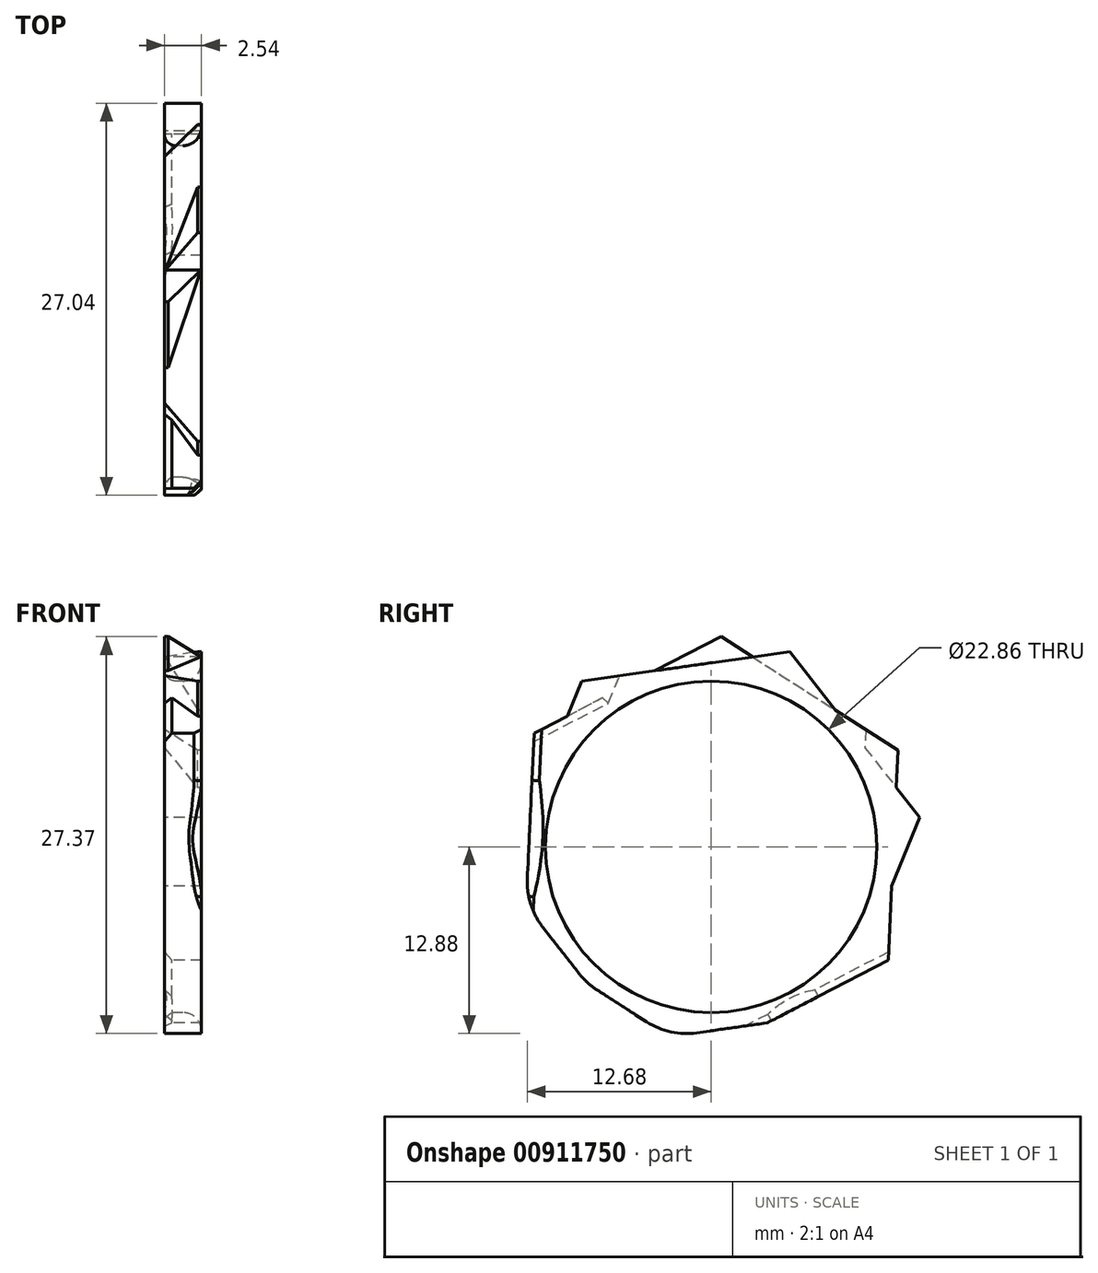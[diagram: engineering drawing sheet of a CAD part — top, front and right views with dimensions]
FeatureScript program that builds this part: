
annotation { "Feature Type Name" : "Feature", "Feature Type Description" : "" }
export const myFeature = defineFeature(function(context is Context, id is Id, definition is map)
    precondition{}
    {
        {
            var Q0;
            Q0=qCreatedBy(makeId("Right.planeOp"),FACE);
            var sketch = newSketch(context, id + "F0", { "sketchPlane" : qUnion([Q0])});
            skCircle(sketch, "E0", {"center": v(0, 0) * mm, "radius": 11.43 * mm});
            skCircle(sketch, "E1.cCircle", {"center": v(0, 0) * mm, "radius": 12.56 * mm, "construction": true});
            skLineSegment(sketch, "E1.0", {"start": v(0.68, 14.49) * mm, "end": v(12.89, 6.66) * mm});
            skLineSegment(sketch, "E1.1", {"start": v(12.89, 6.66) * mm, "end": v(12.2, -7.83) * mm});
            skLineSegment(sketch, "E1.2", {"start": v(12.2, -7.83) * mm, "end": v(-0.68, -14.49) * mm});
            skLineSegment(sketch, "E1.3", {"start": v(-0.68, -14.49) * mm, "end": v(-12.89, -6.66) * mm});
            skLineSegment(sketch, "E1.4", {"start": v(-12.89, -6.66) * mm, "end": v(-12.2, 7.83) * mm});
            skLineSegment(sketch, "E1.5", {"start": v(-12.2, 7.83) * mm, "end": v(0.68, 14.49) * mm});
            skPoint(sketch, "E1.0.midPoint", {"position": v(6.78, 10.57) * mm});
            skLineSegment(sketch, "E2.0", {"start": v(-8.94, 11.42) * mm, "end": v(5.42, 13.45) * mm});
            skLineSegment(sketch, "E2.1", {"start": v(5.42, 13.45) * mm, "end": v(14.36, 2.04) * mm});
            skLineSegment(sketch, "E2.2", {"start": v(14.36, 2.04) * mm, "end": v(8.94, -11.42) * mm});
            skLineSegment(sketch, "E2.3", {"start": v(8.94, -11.42) * mm, "end": v(-5.42, -13.45) * mm});
            skLineSegment(sketch, "E2.4", {"start": v(-5.42, -13.45) * mm, "end": v(-14.36, -2.04) * mm});
            skLineSegment(sketch, "E2.5", {"start": v(-14.36, -2.04) * mm, "end": v(-8.94, 11.42) * mm});
            skPoint(sketch, "E2.0.midPoint", {"position": v(-1.76, 12.44) * mm});
            skSolve(sketch);
        }
        {
            var Q0;
            Q0=makeQuery(id+"F0.imprint","IMPRINT",FACE,{"disambiguationData":[TD([[makeQuery(id+"F0.imprint","IMPRINT",EDGE,{"derivedFrom":sQuery(id+"F0.wireOp",EDGE,"E0")}),-1.0]])]});
            var Q1;
            {var subQ0=sQuery(id+"F0.wireOp",EDGE,"E2.1");var subQ1=sQuery(id+"F0.wireOp",EDGE,"E1.1");var subQ2=makeQuery(id+"F0.imprint","INTERSECT",VERTEX,{"derivedFrom":[subQ1,subQ0]});Q1=makeQuery(id+"F0.imprint","IMPRINT",FACE,{"disambiguationData":[TD([[makeQuery(id+"F0.imprint","IMPRINT",EDGE,{"disambiguationData":[TD([[subQ2,-1.0]])],"derivedFrom":subQ1}),1.0]])]});}
            var Q2;
            {var subQ0=sQuery(id+"F0.wireOp",EDGE,"E1.1");var subQ1=sQuery(id+"F0.wireOp",EDGE,"E1.0");var subQ2=makeQuery(id+"F0.imprint","INTERSECT",VERTEX,{"derivedFrom":[subQ1,subQ0]});Q2=makeQuery(id+"F0.imprint","IMPRINT",FACE,{"disambiguationData":[TD([[makeQuery(id+"F0.imprint","IMPRINT",EDGE,{"disambiguationData":[TD([[subQ2,1.0]])],"derivedFrom":subQ1}),-1.0]])]});}
            var Q3;
            {var subQ0=sQuery(id+"F0.wireOp",EDGE,"E2.0");var subQ1=sQuery(id+"F0.wireOp",EDGE,"E1.0");var subQ2=makeQuery(id+"F0.imprint","INTERSECT",VERTEX,{"derivedFrom":[subQ1,subQ0]});Q3=makeQuery(id+"F0.imprint","IMPRINT",FACE,{"disambiguationData":[TD([[makeQuery(id+"F0.imprint","IMPRINT",EDGE,{"disambiguationData":[TD([[subQ2,-1.0]])],"derivedFrom":subQ1}),1.0]])]});}
            var Q4;
            {var subQ0=sQuery(id+"F0.wireOp",EDGE,"E1.5");var subQ1=sQuery(id+"F0.wireOp",EDGE,"E1.0");var subQ2=makeQuery(id+"F0.imprint","INTERSECT",VERTEX,{"derivedFrom":[subQ1,subQ0]});Q4=makeQuery(id+"F0.imprint","IMPRINT",FACE,{"disambiguationData":[TD([[makeQuery(id+"F0.imprint","IMPRINT",EDGE,{"disambiguationData":[TD([[subQ2,-1.0]])],"derivedFrom":subQ1}),-1.0]])]});}
            var Q5;
            {var subQ0=sQuery(id+"F0.wireOp",EDGE,"E2.5");var subQ1=sQuery(id+"F0.wireOp",EDGE,"E1.5");var subQ2=makeQuery(id+"F0.imprint","INTERSECT",VERTEX,{"derivedFrom":[subQ1,subQ0]});Q5=makeQuery(id+"F0.imprint","IMPRINT",FACE,{"disambiguationData":[TD([[makeQuery(id+"F0.imprint","IMPRINT",EDGE,{"disambiguationData":[TD([[subQ2,-1.0]])],"derivedFrom":subQ1}),1.0]])]});}
            var Q6;
            {var subQ0=sQuery(id+"F0.wireOp",EDGE,"E1.5");var subQ1=sQuery(id+"F0.wireOp",EDGE,"E1.4");var subQ2=makeQuery(id+"F0.imprint","INTERSECT",VERTEX,{"derivedFrom":[subQ1,subQ0]});Q6=makeQuery(id+"F0.imprint","IMPRINT",FACE,{"disambiguationData":[TD([[makeQuery(id+"F0.imprint","IMPRINT",EDGE,{"disambiguationData":[TD([[subQ2,1.0]])],"derivedFrom":subQ1}),-1.0]])]});}
            var Q7;
            {var subQ0=sQuery(id+"F0.wireOp",EDGE,"E1.2");var subQ1=sQuery(id+"F0.wireOp",EDGE,"E1.1");var subQ2=makeQuery(id+"F0.imprint","INTERSECT",VERTEX,{"derivedFrom":[subQ1,subQ0]});Q7=makeQuery(id+"F0.imprint","IMPRINT",FACE,{"disambiguationData":[TD([[makeQuery(id+"F0.imprint","IMPRINT",EDGE,{"disambiguationData":[TD([[subQ2,1.0]])],"derivedFrom":subQ1}),-1.0]])]});}
            extrude(context, id + "F1", {"entities" : qUnion([Q0, Q1, Q2, Q3, Q4, Q5, Q6, Q7]), "depth" : 2.54 * mm, "offsetDistance" : 25.4 * mm});
        }
        {
            var Q0;
            {var subQ0=sQuery(id+"F0.wireOp",EDGE,"E2.1");Q0=makeQuery(id+"F1.opExtrude","CAP_EDGE",EDGE,{"disambiguationData":[OSD([subQ0]),TDD([makeQuery(id+"F0.imprint","IMPRINT",EDGE,{"disambiguationData":[TD([[makeQuery(id+"F0.imprint","INTERSECT",VERTEX,{"derivedFrom":[sQuery(id+"F0.wireOp",EDGE,"E2.0"),subQ0]}),-1.0]])],"derivedFrom":subQ0})])],"isStart":true});}
            var Q1;
            {var subQ0=sQuery(id+"F0.wireOp",EDGE,"E1.5");Q1=makeQuery(id+"F1.opExtrude","CAP_EDGE",EDGE,{"disambiguationData":[OSD([subQ0]),TDD([makeQuery(id+"F0.imprint","IMPRINT",EDGE,{"disambiguationData":[TD([[makeQuery(id+"F0.imprint","INTERSECT",VERTEX,{"derivedFrom":[sQuery(id+"F0.wireOp",EDGE,"E1.0"),subQ0]}),1.0]])],"derivedFrom":subQ0})])],"isStart":false});}
            var Q2;
            {var subQ0=sQuery(id+"F0.wireOp",EDGE,"E1.1");Q2=makeQuery(id+"F1.opExtrude","CAP_EDGE",EDGE,{"disambiguationData":[OSD([subQ0]),TDD([makeQuery(id+"F0.imprint","IMPRINT",EDGE,{"disambiguationData":[TD([[makeQuery(id+"F0.imprint","INTERSECT",VERTEX,{"derivedFrom":[sQuery(id+"F0.wireOp",EDGE,"E1.0"),subQ0]}),-1.0]])],"derivedFrom":subQ0})])],"isStart":true});}
            var Q3;
            Q3=makeQuery(id+"F1.opExtrude","CAP_EDGE",EDGE,{"disambiguationData":[OSD([sQuery(id+"F0.wireOp",EDGE,"E2.5")])],"isStart":true});
            chamfer(context, id + "F2", {"entities" : qUnion([Q0, Q1, Q2, Q3]), "width" : 2.3 * mm, "tangentPropagation" : true});
        }
        {
            var Q0;
            Q0=makeQuery(id+"F1.opExtrude","CAP_EDGE",EDGE,{"disambiguationData":[OSD([sQuery(id+"F0.wireOp",EDGE,"E0")])],"isStart":false});
            fillet(context, id + "F3", {"entities" : qUnion([Q0]), "radius" : 1.27 * mm, "tangentPropagation" : true, "allowEdgeOverflow" : false});
        }
        {
            var Q0;
            Q0=makeQuery(id+"F1.opExtrude","CAP_EDGE",EDGE,{"disambiguationData":[OSD([sQuery(id+"F0.wireOp",EDGE,"E0")])],"isStart":true});
            fillet(context, id + "F4", {"entities" : qUnion([Q0]), "radius" : 0.76 * mm, "tangentPropagation" : true, "allowEdgeOverflow" : false});
        }
        {
            var Q0;
            Q0=makeQuery(id+"F1.opExtrude","CAP_EDGE",EDGE,{"disambiguationData":[OSD([sQuery(id+"F0.wireOp",EDGE,"E1.4")])],"isStart":false});
            var Q1;
            {var subQ0=sQuery(id+"F0.wireOp",EDGE,"E1.5");Q1=makeQuery(id+"F1.opExtrude","CAP_EDGE",EDGE,{"disambiguationData":[OSD([subQ0]),TDD([makeQuery(id+"F0.imprint","IMPRINT",EDGE,{"disambiguationData":[TD([[makeQuery(id+"F0.imprint","INTERSECT",VERTEX,{"derivedFrom":[sQuery(id+"F0.wireOp",EDGE,"E1.4"),subQ0]}),-1.0]])],"derivedFrom":subQ0})])],"isStart":true});}
            var Q2;
            Q2=makeQuery(id+"F1.opExtrude","CAP_EDGE",EDGE,{"disambiguationData":[OSD([sQuery(id+"F0.wireOp",EDGE,"E1.2")])],"isStart":true});
            chamfer(context, id + "F5", {"entities" : qUnion([Q0, Q1, Q2]), "width" : 0.5 * mm, "tangentPropagation" : true});
        }
        {
            var Q0;
            Q0=makeQuery(id+"F1.opExtrude","SWEPT_EDGE",EDGE,{"disambiguationData":[OSD([sQuery(id+"F0.wireOp",EDGE,"E1.3"),sQuery(id+"F0.wireOp",EDGE,"E2.3")])]});
            var Q1;
            Q1=makeQuery(id+"F1.opExtrude","SWEPT_EDGE",EDGE,{"disambiguationData":[OSD([sQuery(id+"F0.wireOp",EDGE,"E1.3"),sQuery(id+"F0.wireOp",EDGE,"E2.4")])]});
            var Q2;
            Q2=makeQuery(id+"F1.opExtrude","SWEPT_EDGE",EDGE,{"disambiguationData":[OSD([sQuery(id+"F0.wireOp",EDGE,"E1.4"),sQuery(id+"F0.wireOp",EDGE,"E2.4")])]});
            fillet(context, id + "F6", {"entities" : qUnion([Q0, Q1, Q2]), "radius" : 5.08 * mm, "tangentPropagation" : true, "allowEdgeOverflow" : false});
        }
    });
